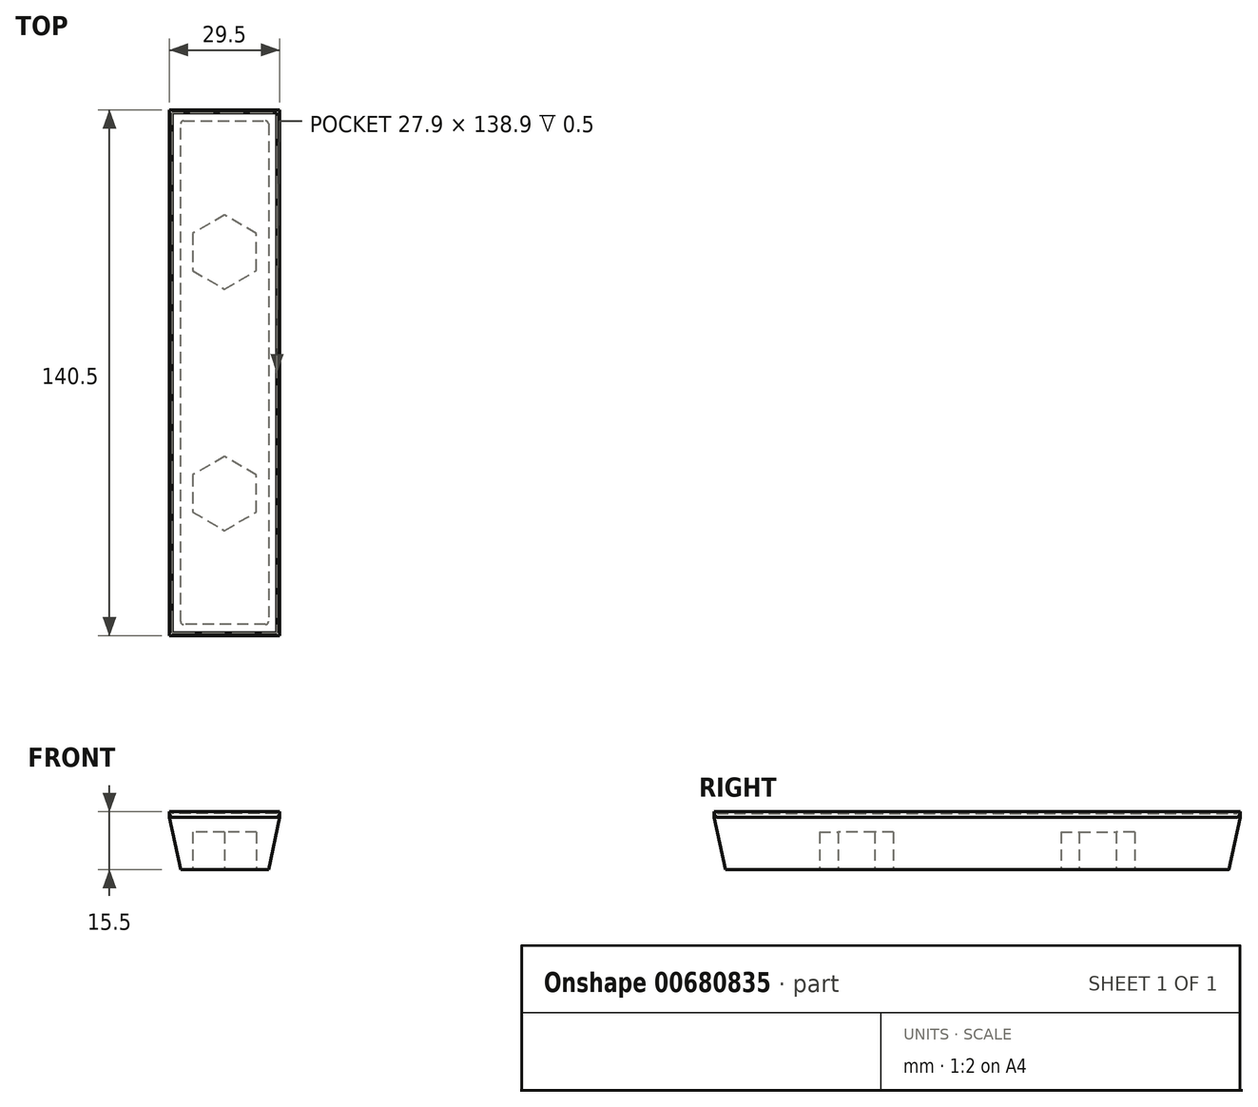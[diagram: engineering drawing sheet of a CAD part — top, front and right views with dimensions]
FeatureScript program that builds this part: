
annotation { "Feature Type Name" : "Feature", "Feature Type Description" : "" }
export const myFeature = defineFeature(function(context is Context, id is Id, definition is map)
    precondition{}
    {
        {
            assignVariable(context, id + "F0", {"name" : "h", "anyValue" : 15});
        }
        {
            var Q0;
            Q0=qCreatedBy(makeId("Top.planeOp"),FACE);
            var sketch = newSketch(context, id + "F1", { "sketchPlane" : qUnion([Q0])});
            skLineSegment(sketch, "E0.bottom", {"start": v(-14.75, -70.25) * mm, "end": v(14.75, -70.25) * mm});
            skLineSegment(sketch, "E0.top", {"start": v(-14.75, 70.25) * mm, "end": v(14.75, 70.25) * mm});
            skLineSegment(sketch, "E0.left", {"start": v(-14.75, -70.25) * mm, "end": v(-14.75, 70.25) * mm});
            skLineSegment(sketch, "E0.right", {"start": v(14.75, -70.25) * mm, "end": v(14.75, 70.25) * mm});
            skPoint(sketch, "E0.middle", {"position": v(0, 0) * mm});
            skLineSegment(sketch, "E1.bottom", {"start": v(13.95, -69.45) * mm, "end": v(-13.95, -69.45) * mm});
            skLineSegment(sketch, "E1.top", {"start": v(13.95, 69.45) * mm, "end": v(-13.95, 69.45) * mm});
            skLineSegment(sketch, "E1.left", {"start": v(13.95, -69.45) * mm, "end": v(13.95, 69.45) * mm});
            skLineSegment(sketch, "E1.right", {"start": v(-13.95, -69.45) * mm, "end": v(-13.95, 69.45) * mm});
            skSolve(sketch);
        }
        {
            var Q0;
            Q0 = qSketchRegion(id + "F1", true);
            extrude(context, id + "F2", {"entities" : qUnion([Q0]), "depth" : 0.5 * mm, "offsetDistance" : 25 * mm});
        }
        {
            var Q0;
            Q0 = qSketchRegion(id + "F1", true);
            var Q1;
            Q1=makeQuery(id+"F1.imprint","IMPRINT",FACE,{"disambiguationData":[TD([[makeQuery(id+"F1.imprint","IMPRINT",EDGE,{"derivedFrom":sQuery(id+"F1.wireOp",EDGE,"E1.bottom")}),-1.0]])]});
            extrude(context, id + "F3", {"entities" : qUnion([Q0, Q1]), "operationType" : NewBodyOperationType.ADD, "depth" : (-getVariable(context, 'h')) * mm, "offsetDistance" : 25 * mm});
        }
        {
            var Q0;
            Q0=makeQuery(id+"F3.opExtrude","CAP_EDGE",EDGE,{"disambiguationData":[OSD([sQuery(id+"F1.wireOp",EDGE,"E0.bottom")])],"isStart":false});
            var Q1;
            Q1=makeQuery(id+"F3.opExtrude","CAP_EDGE",EDGE,{"disambiguationData":[OSD([sQuery(id+"F1.wireOp",EDGE,"E0.right")])],"isStart":false});
            var Q2;
            Q2=makeQuery(id+"F3.opExtrude","CAP_EDGE",EDGE,{"disambiguationData":[OSD([sQuery(id+"F1.wireOp",EDGE,"E0.top")])],"isStart":false});
            var Q3;
            Q3=makeQuery(id+"F3.opExtrude","CAP_EDGE",EDGE,{"disambiguationData":[OSD([sQuery(id+"F1.wireOp",EDGE,"E0.left")])],"isStart":false});
            chamfer(context, id + "F4", {"entities" : qUnion([Q0, Q1, Q2, Q3]), "chamferType" : ChamferType.TWO_OFFSETS, "width1" : (getVariable(context, 'h') - 1) * mm, "oppositeDirection" : false, "width2" : 3 * mm, "tangentPropagation" : true});
        }
        {
            var Q0;
            Q0=makeQuery(id+"F4.opChamfer","BLEND_EDGE",EDGE,{"blendedFrom":[makeQuery(id+"F3.opExtrude","CAP_EDGE",EDGE,{"disambiguationData":[OSD([sQuery(id+"F1.wireOp",EDGE,"E0.top")])],"isStart":false}),makeQuery(id+"F3.opExtrude","CAP_EDGE",EDGE,{"disambiguationData":[OSD([sQuery(id+"F1.wireOp",EDGE,"E0.right")])],"isStart":false})],"blendedInto":[]});
            var Q1;
            Q1=makeQuery(id+"F4.opChamfer","BLEND_EDGE",EDGE,{"blendedFrom":[makeQuery(id+"F3.opExtrude","CAP_EDGE",EDGE,{"disambiguationData":[OSD([sQuery(id+"F1.wireOp",EDGE,"E0.top")])],"isStart":false}),makeQuery(id+"F3.opExtrude","CAP_EDGE",EDGE,{"disambiguationData":[OSD([sQuery(id+"F1.wireOp",EDGE,"E0.left")])],"isStart":false})],"blendedInto":[]});
            var Q2;
            Q2=makeQuery(id+"F4.opChamfer","BLEND_EDGE",EDGE,{"blendedFrom":[makeQuery(id+"F3.opExtrude","CAP_EDGE",EDGE,{"disambiguationData":[OSD([sQuery(id+"F1.wireOp",EDGE,"E0.bottom")])],"isStart":false}),makeQuery(id+"F3.opExtrude","CAP_EDGE",EDGE,{"disambiguationData":[OSD([sQuery(id+"F1.wireOp",EDGE,"E0.right")])],"isStart":false})],"blendedInto":[]});
            var Q3;
            Q3=makeQuery(id+"F4.opChamfer","BLEND_EDGE",EDGE,{"blendedFrom":[makeQuery(id+"F3.opExtrude","CAP_EDGE",EDGE,{"disambiguationData":[OSD([sQuery(id+"F1.wireOp",EDGE,"E0.bottom")])],"isStart":false}),makeQuery(id+"F3.opExtrude","CAP_EDGE",EDGE,{"disambiguationData":[OSD([sQuery(id+"F1.wireOp",EDGE,"E0.left")])],"isStart":false})],"blendedInto":[]});
            fillet(context, id + "F5", {"entities" : qUnion([Q0, Q1, Q2, Q3]), "radius" : 0.8 * mm, "tangentPropagation" : true, "allowEdgeOverflow" : false});
        }
        {
            var Q0;
            Q0=makeQuery(id+"F3.opExtrude","CAP_FACE",FACE,{"disambiguationData":[OSD([sQuery(id+"F1.wireOp",EDGE,"E0.bottom"),sQuery(id+"F1.wireOp",EDGE,"E0.top"),sQuery(id+"F1.wireOp",EDGE,"E0.left"),sQuery(id+"F1.wireOp",EDGE,"E0.right")])],"isStart":false});
            var sketch = newSketch(context, id + "F6", { "sketchPlane" : qUnion([Q0])});
            skLineSegment(sketch, "E2", {"start": v(0, -67.25) * mm, "end": v(0, 67.25) * mm, "construction": true});
            skCircle(sketch, "E3.cCircle", {"center": v(0, -32.25) * mm, "radius": 8.55 * mm, "construction": true});
            skLineSegment(sketch, "E3.0", {"start": v(0, -42.12) * mm, "end": v(-8.55, -37.19) * mm});
            skLineSegment(sketch, "E3.1", {"start": v(-8.55, -37.19) * mm, "end": v(-8.55, -27.31) * mm});
            skLineSegment(sketch, "E3.2", {"start": v(-8.55, -27.31) * mm, "end": v(0, -22.38) * mm});
            skLineSegment(sketch, "E3.3", {"start": v(0, -22.38) * mm, "end": v(8.55, -27.31) * mm});
            skLineSegment(sketch, "E3.4", {"start": v(8.55, -27.31) * mm, "end": v(8.55, -37.19) * mm});
            skLineSegment(sketch, "E3.5", {"start": v(8.55, -37.19) * mm, "end": v(0, -42.12) * mm});
            skPoint(sketch, "E3.0.midPoint", {"position": v(-4.28, -39.65) * mm});
            skCircle(sketch, "E4.cCircle", {"center": v(0, 32.25) * mm, "radius": 8.55 * mm, "construction": true});
            skLineSegment(sketch, "E4.0", {"start": v(-8.55, 27.31) * mm, "end": v(-8.55, 37.19) * mm});
            skLineSegment(sketch, "E4.1", {"start": v(-8.55, 37.19) * mm, "end": v(0, 42.12) * mm});
            skLineSegment(sketch, "E4.2", {"start": v(0, 42.12) * mm, "end": v(8.55, 37.19) * mm});
            skLineSegment(sketch, "E4.3", {"start": v(8.55, 37.19) * mm, "end": v(8.55, 27.31) * mm});
            skLineSegment(sketch, "E4.4", {"start": v(8.55, 27.31) * mm, "end": v(0, 22.38) * mm});
            skLineSegment(sketch, "E4.5", {"start": v(0, 22.38) * mm, "end": v(-8.55, 27.31) * mm});
            skPoint(sketch, "E4.0.midPoint", {"position": v(-8.55, 32.25) * mm});
            skSolve(sketch);
        }
        {
            var Q0;
            Q0=makeQuery(id+"F6.imprint","IMPRINT",FACE,{"disambiguationData":[TD([[makeQuery(id+"F6.imprint","IMPRINT",EDGE,{"derivedFrom":sQuery(id+"F6.wireOp",EDGE,"E4.0")}),-1.0]])]});
            var Q1;
            Q1=makeQuery(id+"F6.imprint","IMPRINT",FACE,{"disambiguationData":[TD([[makeQuery(id+"F6.imprint","IMPRINT",EDGE,{"derivedFrom":sQuery(id+"F6.wireOp",EDGE,"E3.0")}),-1.0]])]});
            extrude(context, id + "F7", {"entities" : qUnion([Q0, Q1]), "operationType" : NewBodyOperationType.REMOVE, "oppositeDirection" : true, "depth" : 10 * mm, "offsetDistance" : 25 * mm});
        }
    });
